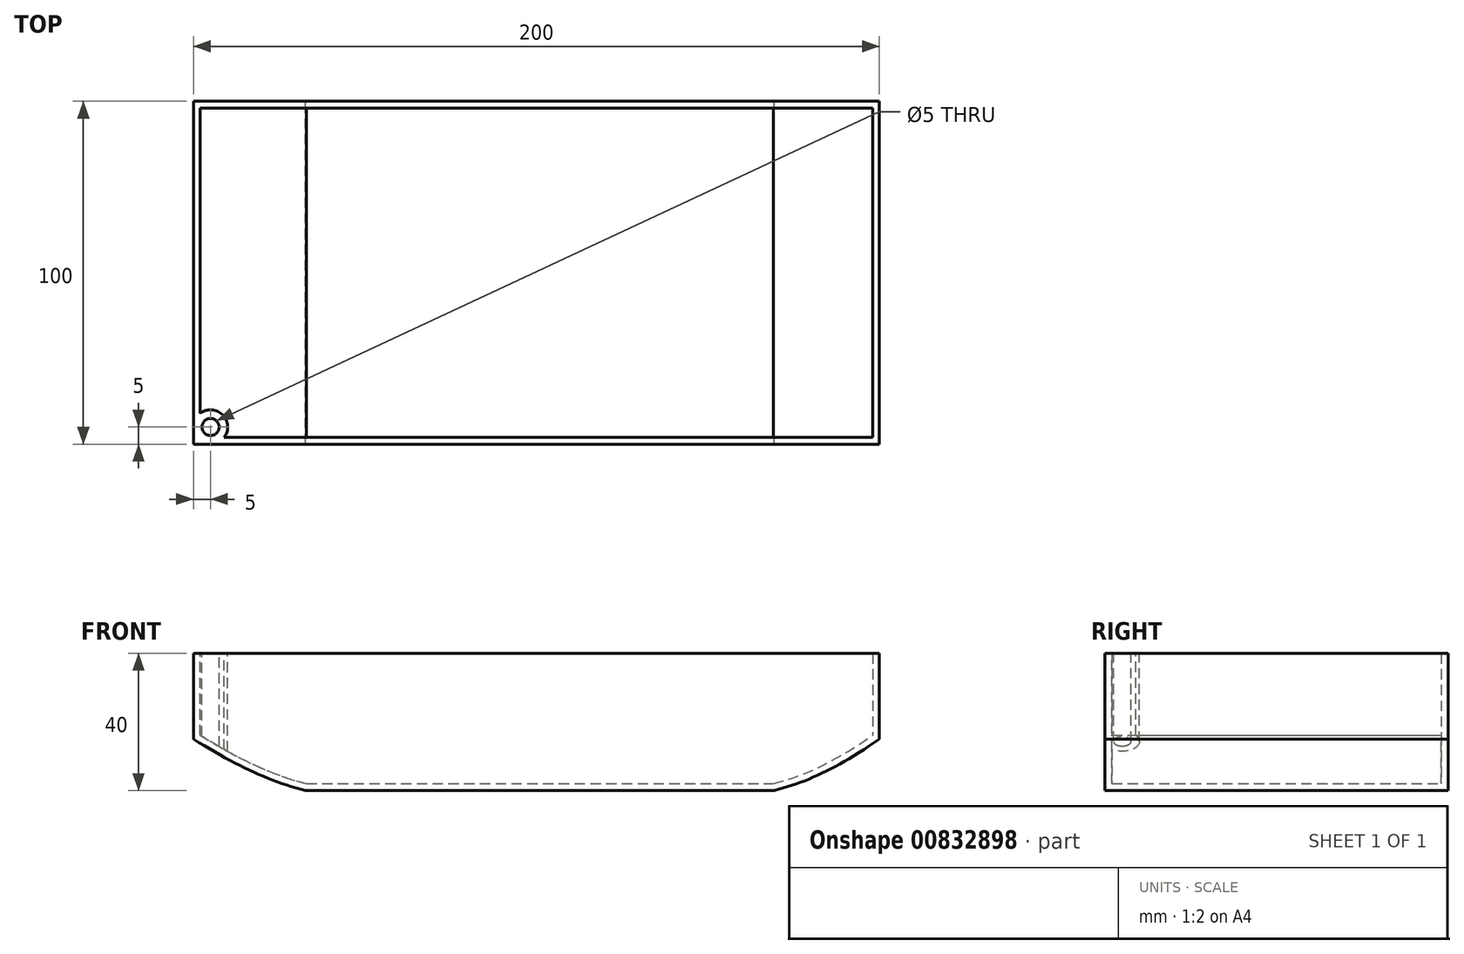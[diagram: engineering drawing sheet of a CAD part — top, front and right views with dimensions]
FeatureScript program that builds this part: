
annotation { "Feature Type Name" : "Feature", "Feature Type Description" : "" }
export const myFeature = defineFeature(function(context is Context, id is Id, definition is map)
    precondition{}
    {
        {
            var Q0;
            Q0=qCreatedBy(makeId("Front.planeOp"),FACE);
            var sketch = newSketch(context, id + "F0", { "sketchPlane" : qUnion([Q0])});
            skLineSegment(sketch, "E0.bottom", {"start": v(-100, 20) * mm, "end": v(100, 20) * mm});
            skLineSegment(sketch, "E0.top", {"start": v(-67.3, -20) * mm, "end": v(69.35, -20) * mm});
            skLineSegment(sketch, "E0.left", {"start": v(-100, 20) * mm, "end": v(-100, -5) * mm});
            skLineSegment(sketch, "E0.right", {"start": v(100, 20) * mm, "end": v(100, -5) * mm});
            skFitSpline(sketch, "E1", {"points": [v(-100, -5) * mm, v(-50, -23) * mm, v(50, -23) * mm, v(100, -5) * mm], "startDerivative": vector(187.98, -116.1) * mm, "endDerivative": vector(192, 132.6) * mm});
            skPoint(sketch, "E2.orphan", {"position": v(-100, -20) * mm});
            skPoint(sketch, "E3.orphan", {"position": v(100, -20) * mm});
            skSolve(sketch);
        }
        {
            var Q0;
            Q0=makeQuery(id+"F0.imprint","IMPRINT",FACE,{"disambiguationData":[TD([[makeQuery(id+"F0.imprint","IMPRINT",EDGE,{"derivedFrom":sQuery(id+"F0.wireOp",EDGE,"E0.bottom")}),-1.0]])]});
            extrude(context, id + "F1", {"entities" : qUnion([Q0]), "endBound" : BoundingType.SYMMETRIC, "depth" : 100 * mm, "offsetDistance" : 25 * mm});
        }
        {
            var Q0;
            Q0=makeQuery(id+"F1.opExtrude","SWEPT_FACE",FACE,{"disambiguationData":[OSD([sQuery(id+"F0.wireOp",EDGE,"E0.bottom")])]});
            shell(context, id + "F2", {"entities" : qUnion([Q0]), "thickness" : 2 * mm});
        }
        {
            var Q0;
            Q0=makeQuery(id+"F1.opExtrude","SWEPT_FACE",FACE,{"disambiguationData":[OSD([sQuery(id+"F0.wireOp",EDGE,"E0.bottom")])]});
            var sketch = newSketch(context, id + "F3", { "sketchPlane" : qUnion([Q0])});
            skCircle(sketch, "E4", {"center": v(-95, -45) * mm, "radius": 2.5 * mm});
            skCircle(sketch, "E5", {"center": v(-95, -45) * mm, "radius": 5 * mm});
            skSolve(sketch);
        }
        {
            var Q0;
            Q0=makeQuery(id+"F3.imprint","IMPRINT",FACE,{"disambiguationData":[TD([[makeQuery(id+"F3.imprint","IMPRINT",EDGE,{"derivedFrom":sQuery(id+"F3.wireOp",EDGE,"E4")}),-1.0]])]});
            extrude(context, id + "F4", {"entities" : qUnion([Q0]), "operationType" : NewBodyOperationType.ADD, "endBound" : BoundingType.UP_TO_NEXT, "oppositeDirection" : true, "depth" : 25 * mm, "offsetDistance" : 25 * mm});
        }
    });
